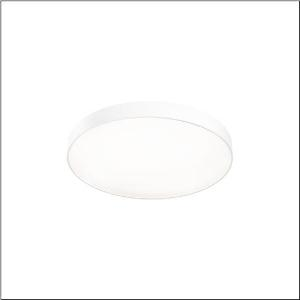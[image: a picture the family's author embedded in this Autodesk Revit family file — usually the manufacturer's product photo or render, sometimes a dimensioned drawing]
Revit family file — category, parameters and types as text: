
# Revit family: round_21_m_51mr36gm8421w
name_source: partatom
category: Lighting Fixtures
units: mm (PartAtom-declared; Revit-internal decimal feet)

## family parameters
Cut with Voids When Loaded = No
Host = Face
Light Source = No
Part Type = Normal
Room Calculation Point = No
Round Connector Dimension = Use Diameter
Shared = No

## types (1)
- --- (1 x LED, 8190 lm, 60.8 W, 4000K)
    Apparent Load = 61 VA
    CIE Flux Codes = 49 80 96 85 100
    Color Rendering = 80
    Color Temperature = 4000K
    Default Elevation = 1800 mm
    Description = Round 21 M, wall and ceiling luminaire, primary optical cover: cover, of PMMA, opal, light emission: direct/indirect distribution, primary light characteristic: symmetric, installation type: suspended mounting, surface-mounted, LED, rated luminous flux: 8.190lm, luminous efficacy: 135lm/W, light colour: 840, colour temperature: 4000K, with terminal, 3-pole, mains connection: 230V, AC, 50/60Hz, rated input power: 61W, housing, of aluminium, coated, white, diameter: 600mm, height: 62mm, protection rating (complete): IP40, insulation class (complete): insulation class I (protective earthing), certification: CE, impact resistance: IK04, permissible operating ambient temperature: -10..+35°C, packaging unit: 1 piece
    Height = 87 mm
    Lamp = 1 x LED
    Lamp Light Flux = 8190 lm
    Lamp Power = 60.8 W
    Lamp count = 1
    Length = 600 mm
    Luminous efficacy = 135 lm/W
    Manufacturer = Siteco
    ModVariant = No
    Model = 51MR36GM8421W
    Mounting Place = Ceiling
    Mounting Type = Surface mounted
    Number of Poles = 1
    OnlyDefault = Yes
    Power Factor = 1
    Product Name = Round 21 M
    Product group = wall and ceiling luminaire
    ProductGroupID = 301
    Protection Class = Protection class I
    Protection Degree = IP 40
    RLX_Detail_Level = 1
    RLX_Emergency_Light_Flux = 0 lm
    RLX_Emergency_Type = 0
    RLX_Emergency_Type_DB = No
    RlxData = <blob elided: 14753 chars, md5=caf8a147>
    Socket = socket
    Standby Power = 0 W
    System Light Flux = 8190 lm
    System Power = 61 W
    Type Comments = factory setting: luminous flux: 100 % | (ON | ON | ON | ON) | 700 mA
    Type Image = l_1258330.jpg
    URL = http://relux.com
    VarID = @adj_013305
    Voltage = 0 V
    Weight = 0.00 kg
    Width = 0 mm  [stored 0 ft]

note: [stored X ft] marks values corroborated as IEEE doubles in the binary element streams (Revit-internal decimal feet)

## geometry (parser evidence)
native form markers: Sweep x13
no freeform markers — native parametric forms only
